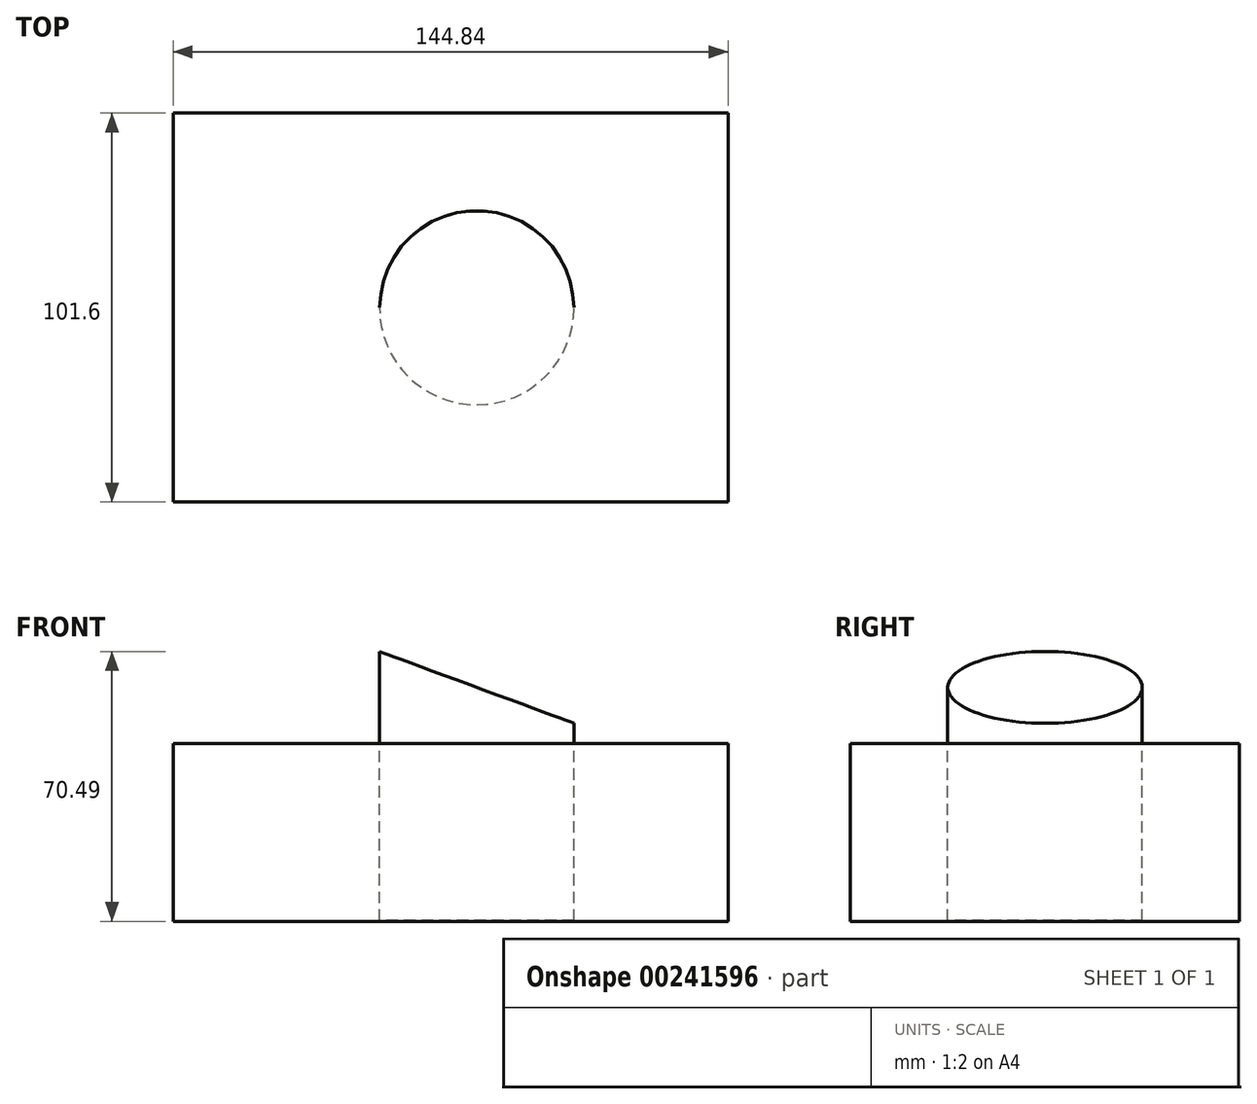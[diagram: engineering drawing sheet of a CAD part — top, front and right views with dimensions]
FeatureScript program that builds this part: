
annotation { "Feature Type Name" : "Feature", "Feature Type Description" : "" }
export const myFeature = defineFeature(function(context is Context, id is Id, definition is map)
    precondition{}
    {
        {
            var Q0;
            Q0=qCreatedBy(makeId("Front.planeOp"),FACE);
            var sketch = newSketch(context, id + "F0", { "sketchPlane" : qUnion([Q0])});
            skLineSegment(sketch, "E0.bottom", {"start": v(65.6, 26.7) * mm, "end": v(-79.24, 26.7) * mm});
            skLineSegment(sketch, "E0.top", {"start": v(65.6, -19.68) * mm, "end": v(-79.24, -19.68) * mm});
            skLineSegment(sketch, "E0.left", {"start": v(65.6, 26.7) * mm, "end": v(65.6, -19.68) * mm});
            skLineSegment(sketch, "E0.right", {"start": v(-79.24, 26.7) * mm, "end": v(-79.24, -19.68) * mm});
            skLineSegment(sketch, "E1.top", {"start": v(-17.5, -19.68) * mm, "end": v(33.3, -19.68) * mm});
            skSolve(sketch);
        }
        {
            var Q0;
            Q0=makeQuery(id+"F0.imprint","IMPRINT",FACE,{"disambiguationData":[TD([[makeQuery(id+"F0.imprint","IMPRINT",EDGE,{"derivedFrom":sQuery(id+"F0.wireOp",EDGE,"E0.bottom")}),1.0]])]});
            extrude(context, id + "F1", {"entities" : qUnion([Q0]), "endBound" : BoundingType.SYMMETRIC, "depth" : 101.6 * mm});
        }
        {
            var Q0;
            Q0=qCreatedBy(makeId("Front.planeOp"),FACE);
            var sketch = newSketch(context, id + "F2", { "sketchPlane" : qUnion([Q0])});
            skLineSegment(sketch, "E2.bottom", {"start": v(-25.4, -19.54) * mm, "end": v(25.4, -19.54) * mm});
            skLineSegment(sketch, "E2.top", {"start": v(-25.4, 50.88) * mm, "end": v(25.4, 50.88) * mm});
            skLineSegment(sketch, "E2.left", {"start": v(-25.4, -19.54) * mm, "end": v(-25.4, 50.88) * mm});
            skLineSegment(sketch, "E2.right", {"start": v(25.4, -19.54) * mm, "end": v(25.4, 50.88) * mm});
            skLineSegment(sketch, "E3", {"start": v(0, 50.88) * mm, "end": v(0, -19.54) * mm});
            skSolve(sketch);
        }
        {
            var Q0;
            {var subQ0=sQuery(id+"F2.wireOp",EDGE,"E2.right");Q0=makeQuery(id+"F2.imprint","IMPRINT",FACE,{"disambiguationData":[TD([[makeQuery(id+"F2.imprint","IMPRINT",EDGE,{"derivedFrom":subQ0}),1.0]])]});}
            var Q1;
            Q1=sQuery(id+"F2.wireOp",EDGE,"E3");
            revolve(context, id + "F3", {"entities" : qUnion([Q0]), "axis" : qUnion([Q1]), "revolveType" : RevolveType.FULL});
        }
        {
            var Q0;
            Q0=qCreatedBy(makeId("Front.planeOp"),FACE);
            var sketch = newSketch(context, id + "F4", { "sketchPlane" : qUnion([Q0])});
            skLineSegment(sketch, "E4.bottom", {"start": v(25.4, 50.93) * mm, "end": v(-25.72, 50.93) * mm});
            skLineSegment(sketch, "E4.left", {"start": v(25.4, 50.93) * mm, "end": v(25.4, 32.03) * mm});
            skLineSegment(sketch, "E5", {"start": v(-25.72, 50.93) * mm, "end": v(25.4, 32.03) * mm});
            skSolve(sketch);
        }
        {
            var Q0;
            Q0 = qSketchRegion(id + "F4", true);
            extrude(context, id + "F5", {"entities" : qUnion([Q0]), "operationType" : NewBodyOperationType.REMOVE, "oppositeDirection" : true, "depth" : 127 * mm, "hasSecondDirection" : true, "secondDirectionOppositeDirection" : false, "secondDirectionDepth" : 25.4 * mm});
        }
    });
